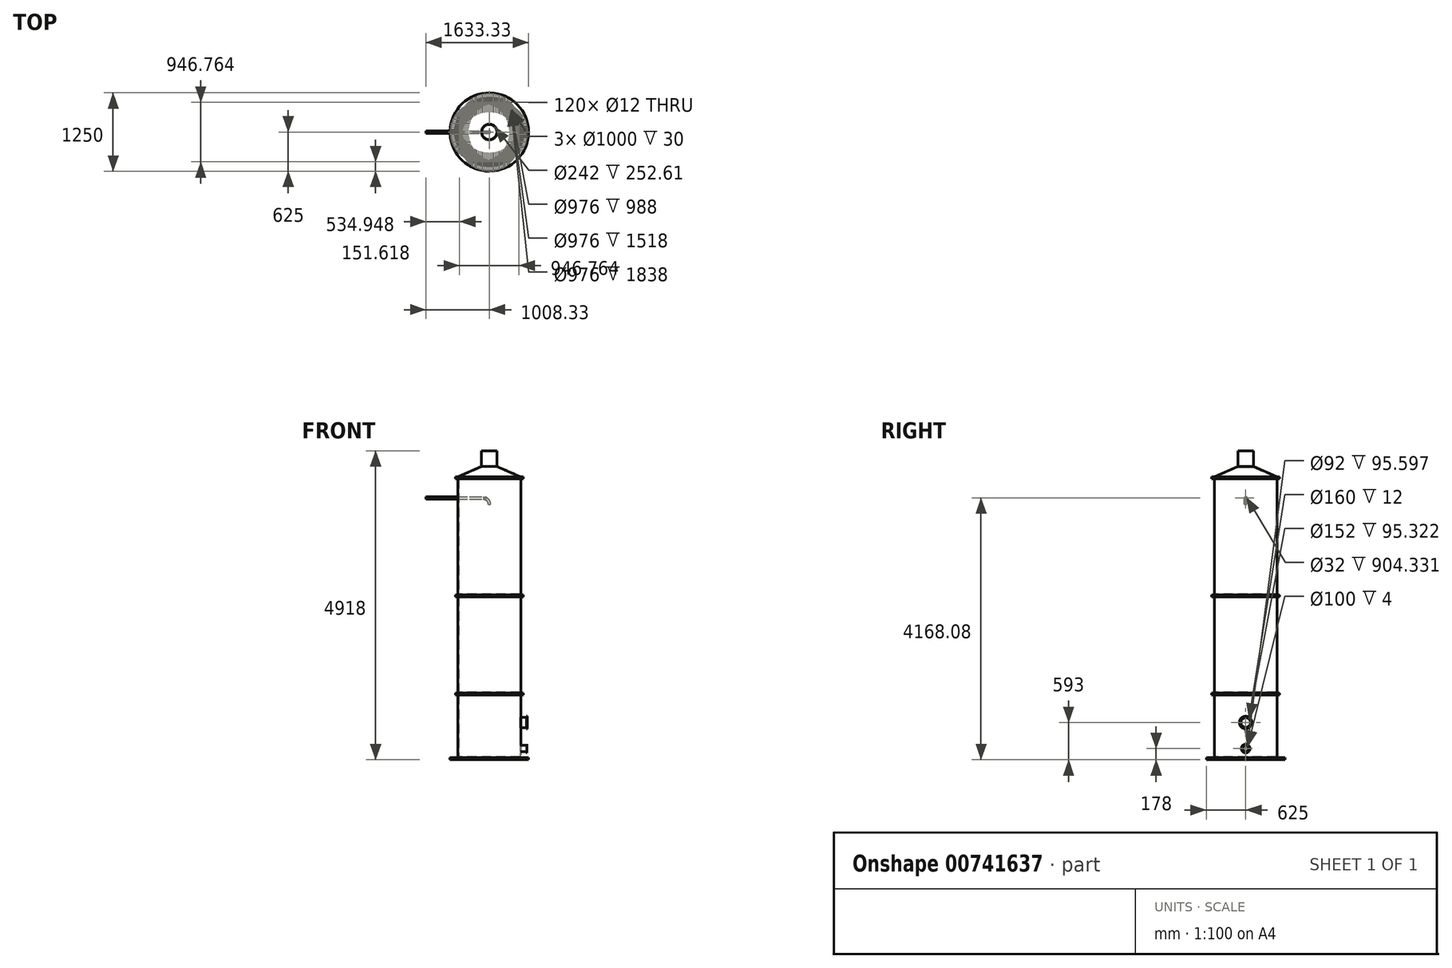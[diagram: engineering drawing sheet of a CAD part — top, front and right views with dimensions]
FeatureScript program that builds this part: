
annotation { "Feature Type Name" : "Feature", "Feature Type Description" : "" }
export const myFeature = defineFeature(function(context is Context, id is Id, definition is map)
    precondition{}
    {
        {
            var Q0;
            Q0=qCreatedBy(makeId("Top.planeOp"),FACE);
            var sketch = newSketch(context, id + "F0", { "sketchPlane" : qUnion([Q0])});
            skCircle(sketch, "E0", {"center": v(0, 0) * mm, "radius": 500 * mm});
            skSolve(sketch);
        }
        {
            var Q0;
            Q0=makeQuery(id+"F0.imprint","IMPRINT",FACE,{"disambiguationData":[TD([[makeQuery(id+"F0.imprint","IMPRINT",EDGE,{"derivedFrom":sQuery(id+"F0.wireOp",EDGE,"E0")}),1.0]])]});
            extrude(context, id + "F1", {"entities" : qUnion([Q0]), "depth" : 1000 * mm, "offsetDistance" : 25 * mm});
        }
        {
            var Q0;
            Q0=makeQuery(id+"F1.opExtrude","CAP_FACE",FACE,{"disambiguationData":[OSD([sQuery(id+"F0.wireOp",EDGE,"E0")])],"isStart":false});
            shell(context, id + "F2", {"entities" : qUnion([Q0]), "thickness" : 12 * mm});
        }
        {
            var Q0;
            {var subQ0=sQuery(id+"F0.wireOp",EDGE,"E0");Q0=makeQuery(id+"F2.opShell","OFFSET_FACE",FACE,{"disambiguationData":[OSD([subQ0]),TDD([makeQuery(id+"F1.opExtrude","CAP_FACE",FACE,{"disambiguationData":[OSD([subQ0])],"isStart":true})])]});}
            cPlane(context, id + "F3", {"entities" : qUnion([Q0]), "cplaneType" : CPlaneType.OFFSET, "offset" : 133 * mm, "width" : 150 * mm, "height" : 150 * mm});
        }
        {
            var Q0;
            Q0=qCreatedBy(id+"F3.planeOp",FACE);
            var sketch = newSketch(context, id + "F4", { "sketchPlane" : qUnion([Q0])});
            skCircle(sketch, "E1", {"center": v(0, 0) * mm, "radius": 500 * mm, "construction": true});
            skLineSegment(sketch, "E2", {"start": v(0, 50) * mm, "end": v(497.5, 50) * mm, "construction": true});
            skLineSegment(sketch, "E3.MirrorCS", {"start": v(0, -50) * mm, "end": v(497.5, -50) * mm, "construction": true});
            skLineSegment(sketch, "E4", {"start": v(497.5, 50) * mm, "end": v(597.5, 50) * mm});
            skLineSegment(sketch, "E5", {"start": v(0, 0) * mm, "end": v(611.46, 0) * mm, "construction": true});
            skArc(sketch, "E6", {"start": v(497.5, 50) * mm, "mid": v(499.37, 25.03) * mm, "end": v(500, 0) * mm});
            skLineSegment(sketch, "E7", {"start": v(500, 0) * mm, "end": v(597.5, 0) * mm});
            skLineSegment(sketch, "E8", {"start": v(597.5, 0) * mm, "end": v(597.5, 50) * mm});
            skSolve(sketch);
        }
        {
            var Q0;
            Q0=makeQuery(id+"F4.imprint","IMPRINT",FACE,{"disambiguationData":[TD([[makeQuery(id+"F4.imprint","IMPRINT",EDGE,{"derivedFrom":sQuery(id+"F4.wireOp",EDGE,"E4")}),-1.0]])]});
            var Q1;
            Q1=sQuery(id+"F4.wireOp",EDGE,"E5");
            revolve(context, id + "F5", {"surfaceOperationType" : NewSurfaceOperationType.NEW, "entities" : qUnion([Q0]), "axis" : qUnion([Q1]), "revolveType" : RevolveType.FULL});
        }
        {
            var Q0;
            Q0=makeQuery(id+"F5.opRevolve","SWEPT_FACE",FACE,{"disambiguationData":[OSD([sQuery(id+"F4.wireOp",EDGE,"E8")])]});
            shell(context, id + "F6", {"entities" : qUnion([Q0]), "thickness" : 4 * mm});
        }
        {
            var Q0;
            Q0=makeQuery(id+"F5.opRevolve","SWEPT_FACE",FACE,{"disambiguationData":[OSD([sQuery(id+"F4.wireOp",EDGE,"E8")])]});
            var sketch = newSketch(context, id + "F7", { "sketchPlane" : qUnion([Q0])});
            skCircle(sketch, "E9.0", {"center": v(0, 145) * mm, "radius": 50 * mm});
            skCircle(sketch, "E10", {"center": v(0, 145) * mm, "radius": 70 * mm});
            skSolve(sketch);
        }
        {
            var Q0;
            Q0=makeQuery(id+"F7.imprint","IMPRINT",FACE,{"disambiguationData":[TD([[makeQuery(id+"F7.imprint","IMPRINT",EDGE,{"derivedFrom":sQuery(id+"F7.wireOp",EDGE,"E9.0")}),1.0]])]});
            var Q1;
            Q1=sQuery(id+"F7.wireOp",EDGE,"E10");
            var Q2;
            Q2=sQuery(id+"F7.wireOp",EDGE,"E9.0");
            extrude(context, id + "F8", {"entities" : qUnion([Q0]), "operationType" : NewBodyOperationType.ADD, "surfaceEntities" : qUnion([Q1, Q2]), "depth" : 4 * mm, "offsetDistance" : 25 * mm});
        }
        {
            var Q0;
            Q0=makeQuery(id+"F1.opExtrude","CAP_FACE",FACE,{"disambiguationData":[OSD([sQuery(id+"F0.wireOp",EDGE,"E0")])],"isStart":true});
            var sketch = newSketch(context, id + "F9", { "sketchPlane" : qUnion([Q0])});
            skCircle(sketch, "E11", {"center": v(0, 0) * mm, "radius": 625 * mm});
            skSolve(sketch);
        }
        {
            var Q0;
            Q0=makeQuery(id+"F9.imprint","IMPRINT",FACE,{"disambiguationData":[TD([[makeQuery(id+"F9.imprint","IMPRINT",EDGE,{"derivedFrom":sQuery(id+"F9.wireOp",EDGE,"E11")}),1.0]])]});
            var Q1;
            Q1=makeQuery(id+"F9.imprint","IMPRINT",FACE,{"disambiguationData":[TD([[makeQuery(id+"F9.imprint","IMPRINT",EDGE,{"derivedFrom":makeQuery(id+"F1.opExtrude","CAP_EDGE",EDGE,{"disambiguationData":[OSD([sQuery(id+"F0.wireOp",EDGE,"E0")])],"isStart":true})}),-1.0]])]});
            var Q2;
            Q2=sQuery(id+"F9.wireOp",EDGE,"E11");
            extrude(context, id + "F10", {"entities" : qUnion([Q0, Q1]), "operationType" : NewBodyOperationType.ADD, "surfaceEntities" : qUnion([Q2]), "depth" : 33 * mm, "offsetDistance" : 25 * mm});
        }
        {
            var Q0;
            Q0=qCreatedBy(id+"F3.planeOp",FACE);
            cPlane(context, id + "F11", {"entities" : qUnion([Q0]), "cplaneType" : CPlaneType.OFFSET, "offset" : 415 * mm, "width" : 150 * mm, "height" : 150 * mm});
        }
        {
            var Q0;
            Q0=qCreatedBy(id+"F11.planeOp",FACE);
            var sketch = newSketch(context, id + "F12", { "sketchPlane" : qUnion([Q0])});
            skCircle(sketch, "E12.0", {"center": v(0, 0) * mm, "radius": 500 * mm});
            skLineSegment(sketch, "E13", {"start": v(0, 0) * mm, "end": v(689.6, 0) * mm, "construction": true});
            skLineSegment(sketch, "E14", {"start": v(0, 80) * mm, "end": v(684.1, 80) * mm, "construction": true});
            skArc(sketch, "E15", {"start": v(493.56, 80) * mm, "mid": v(498.39, 40.13) * mm, "end": v(500, 0) * mm});
            skLineSegment(sketch, "E16", {"start": v(493.56, 80) * mm, "end": v(593.56, 80) * mm});
            skLineSegment(sketch, "E17", {"start": v(593.56, 80) * mm, "end": v(593.56, 0) * mm});
            skLineSegment(sketch, "E18", {"start": v(593.56, 0) * mm, "end": v(500, 0) * mm});
            skSolve(sketch);
        }
        {
            var Q0;
            {var subQ0=sQuery(id+"F12.wireOp",EDGE,"E16");Q0=makeQuery(id+"F12.imprint","IMPRINT",FACE,{"disambiguationData":[TD([[makeQuery(id+"F12.imprint","IMPRINT",EDGE,{"derivedFrom":subQ0}),-1.0]])]});}
            var Q1;
            Q1=sQuery(id+"F12.wireOp",EDGE,"E13");
            revolve(context, id + "F13", {"surfaceOperationType" : NewSurfaceOperationType.NEW, "entities" : qUnion([Q0]), "axis" : qUnion([Q1]), "revolveType" : RevolveType.FULL});
        }
        {
            var Q0;
            Q0=makeQuery(id+"F13.opRevolve","SWEPT_FACE",FACE,{"disambiguationData":[OSD([sQuery(id+"F12.wireOp",EDGE,"E17")])]});
            shell(context, id + "F14", {"entities" : qUnion([Q0]), "thickness" : 4 * mm});
        }
        {
            var Q0;
            Q0=makeQuery(id+"F13.opRevolve","SWEPT_FACE",FACE,{"disambiguationData":[OSD([sQuery(id+"F12.wireOp",EDGE,"E17")])]});
            var sketch = newSketch(context, id + "F15", { "sketchPlane" : qUnion([Q0])});
            skCircle(sketch, "E19", {"center": v(0, 560) * mm, "radius": 100 * mm});
            skSolve(sketch);
        }
        {
            var Q0;
            Q0=makeQuery(id+"F15.imprint","IMPRINT",FACE,{"disambiguationData":[TD([[makeQuery(id+"F15.imprint","IMPRINT",EDGE,{"derivedFrom":sQuery(id+"F15.wireOp",EDGE,"E19")}),1.0]])]});
            extrude(context, id + "F16", {"entities" : qUnion([Q0]), "depth" : 12 * mm, "offsetDistance" : 25 * mm});
        }
        {
            var Q0;
            Q0=makeQuery(id+"F1.opExtrude","CAP_FACE",FACE,{"disambiguationData":[OSD([sQuery(id+"F0.wireOp",EDGE,"E0")])],"isStart":false});
            var sketch = newSketch(context, id + "F17", { "sketchPlane" : qUnion([Q0])});
            skCircle(sketch, "E20", {"center": v(0, 0) * mm, "radius": 540 * mm});
            skCircle(sketch, "E21", {"center": v(0, 0) * mm, "radius": 500 * mm});
            skSolve(sketch);
        }
        {
            var Q0;
            Q0=makeQuery(id+"F17.imprint","IMPRINT",FACE,{"disambiguationData":[TD([[makeQuery(id+"F17.imprint","IMPRINT",EDGE,{"derivedFrom":sQuery(id+"F17.wireOp",EDGE,"E20")}),1.0]])]});
            extrude(context, id + "F18", {"entities" : qUnion([Q0]), "depth" : 30 * mm, "offsetDistance" : 25 * mm});
        }
        {
            var Q0;
            {var subQ0=sQuery(id+"F0.wireOp",EDGE,"E0");Q0=makeQuery(id+"F17.imprint","IMPRINT",FACE,{"disambiguationData":[TD([[makeQuery(id+"F17.imprint","IMPRINT",EDGE,{"derivedFrom":makeQuery(id+"F2.opShell","OFFSET_EDGE",EDGE,{"disambiguationData":[OSD([subQ0]),TDD([makeQuery(id+"F1.opExtrude","CAP_EDGE",EDGE,{"disambiguationData":[OSD([subQ0])],"isStart":false})])]})}),1.0]])]});}
            extrude(context, id + "F19", {"entities" : qUnion([Q0]), "depth" : 12 * mm, "offsetDistance" : 25 * mm});
        }
        {
            var Q0;
            Q0=makeQuery(id+"F19.opExtrude","CAP_FACE",FACE,{"disambiguationData":[OSD([sQuery(id+"F0.wireOp",EDGE,"E0")])],"isStart":false});
            var sketch = newSketch(context, id + "F20", { "sketchPlane" : qUnion([Q0])});
            skLineSegment(sketch, "E22", {"start": v(0, 0) * mm, "end": v(0, 488) * mm, "construction": true});
            skLineSegment(sketch, "E23", {"start": v(0, 0) * mm, "end": v(488, 0) * mm, "construction": true});
            skCircle(sketch, "E24", {"center": v(0, 473.38) * mm, "radius": 6 * mm});
            skCircle(sketch, "E25", {"center": v(0, 0) * mm, "radius": 473.38 * mm, "construction": true});
            skCircle(sketch, "E26.1.0", {"center": v(-24.77, 472.73) * mm, "radius": 6 * mm});
            skCircle(sketch, "E26.2.0", {"center": v(-49.48, 470.79) * mm, "radius": 6 * mm});
            skCircle(sketch, "E26.3.0", {"center": v(-74.05, 467.55) * mm, "radius": 6 * mm});
            skCircle(sketch, "E26.4.0", {"center": v(-98.42, 463.04) * mm, "radius": 6 * mm});
            skCircle(sketch, "E26.5.0", {"center": v(-122.52, 457.25) * mm, "radius": 6 * mm});
            skCircle(sketch, "E26.6.0", {"center": v(-146.28, 450.21) * mm, "radius": 6 * mm});
            skCircle(sketch, "E26.7.0", {"center": v(-169.64, 441.94) * mm, "radius": 6 * mm});
            skCircle(sketch, "E26.8.0", {"center": v(-192.54, 432.46) * mm, "radius": 6 * mm});
            skCircle(sketch, "E26.9.0", {"center": v(-214.91, 421.79) * mm, "radius": 6 * mm});
            skCircle(sketch, "E26.10.0", {"center": v(-236.7, 409.96) * mm, "radius": 6 * mm});
            skCircle(sketch, "E26.11.0", {"center": v(-257.82, 397.01) * mm, "radius": 6 * mm});
            skCircle(sketch, "E26.12.0", {"center": v(-278.25, 382.97) * mm, "radius": 6 * mm});
            skCircle(sketch, "E26.13.0", {"center": v(-297.9, 367.89) * mm, "radius": 6 * mm});
            skCircle(sketch, "E26.14.0", {"center": v(-316.75, 351.8) * mm, "radius": 6 * mm});
            skCircle(sketch, "E26.15.0", {"center": v(-334.73, 334.73) * mm, "radius": 6 * mm});
            skCircle(sketch, "E26.16.0", {"center": v(-351.8, 316.75) * mm, "radius": 6 * mm});
            skCircle(sketch, "E26.17.0", {"center": v(-367.89, 297.9) * mm, "radius": 6 * mm});
            skCircle(sketch, "E26.18.0", {"center": v(-382.97, 278.25) * mm, "radius": 6 * mm});
            skCircle(sketch, "E26.19.0", {"center": v(-397.01, 257.82) * mm, "radius": 6 * mm});
            skCircle(sketch, "E26.20.0", {"center": v(-409.96, 236.7) * mm, "radius": 6 * mm});
            skCircle(sketch, "E26.21.0", {"center": v(-421.79, 214.91) * mm, "radius": 6 * mm});
            skCircle(sketch, "E26.22.0", {"center": v(-432.46, 192.54) * mm, "radius": 6 * mm});
            skCircle(sketch, "E26.23.0", {"center": v(-441.94, 169.64) * mm, "radius": 6 * mm});
            skCircle(sketch, "E26.24.0", {"center": v(-450.21, 146.28) * mm, "radius": 6 * mm});
            skCircle(sketch, "E26.25.0", {"center": v(-457.25, 122.52) * mm, "radius": 6 * mm});
            skCircle(sketch, "E26.26.0", {"center": v(-463.04, 98.42) * mm, "radius": 6 * mm});
            skCircle(sketch, "E26.27.0", {"center": v(-467.55, 74.05) * mm, "radius": 6 * mm});
            skCircle(sketch, "E26.28.0", {"center": v(-470.79, 49.48) * mm, "radius": 6 * mm});
            skCircle(sketch, "E26.29.0", {"center": v(-472.73, 24.77) * mm, "radius": 6 * mm});
            skCircle(sketch, "E26.30.0", {"center": v(-473.38, 0) * mm, "radius": 6 * mm});
            skCircle(sketch, "E26.31.0", {"center": v(-472.73, -24.77) * mm, "radius": 6 * mm});
            skCircle(sketch, "E26.32.0", {"center": v(-470.79, -49.48) * mm, "radius": 6 * mm});
            skCircle(sketch, "E26.33.0", {"center": v(-467.55, -74.05) * mm, "radius": 6 * mm});
            skCircle(sketch, "E26.34.0", {"center": v(-463.04, -98.42) * mm, "radius": 6 * mm});
            skCircle(sketch, "E26.35.0", {"center": v(-457.25, -122.52) * mm, "radius": 6 * mm});
            skCircle(sketch, "E26.36.0", {"center": v(-450.21, -146.28) * mm, "radius": 6 * mm});
            skCircle(sketch, "E26.37.0", {"center": v(-441.94, -169.64) * mm, "radius": 6 * mm});
            skCircle(sketch, "E26.38.0", {"center": v(-432.46, -192.54) * mm, "radius": 6 * mm});
            skCircle(sketch, "E26.39.0", {"center": v(-421.79, -214.91) * mm, "radius": 6 * mm});
            skCircle(sketch, "E26.40.0", {"center": v(-409.96, -236.7) * mm, "radius": 6 * mm});
            skCircle(sketch, "E26.41.0", {"center": v(-397.01, -257.82) * mm, "radius": 6 * mm});
            skCircle(sketch, "E26.42.0", {"center": v(-382.97, -278.25) * mm, "radius": 6 * mm});
            skCircle(sketch, "E26.43.0", {"center": v(-367.89, -297.9) * mm, "radius": 6 * mm});
            skCircle(sketch, "E26.44.0", {"center": v(-351.8, -316.75) * mm, "radius": 6 * mm});
            skCircle(sketch, "E26.45.0", {"center": v(-334.73, -334.73) * mm, "radius": 6 * mm});
            skCircle(sketch, "E26.46.0", {"center": v(-316.75, -351.8) * mm, "radius": 6 * mm});
            skCircle(sketch, "E26.47.0", {"center": v(-297.9, -367.89) * mm, "radius": 6 * mm});
            skCircle(sketch, "E26.48.0", {"center": v(-278.25, -382.97) * mm, "radius": 6 * mm});
            skCircle(sketch, "E26.49.0", {"center": v(-257.82, -397.01) * mm, "radius": 6 * mm});
            skCircle(sketch, "E26.50.0", {"center": v(-236.7, -409.96) * mm, "radius": 6 * mm});
            skCircle(sketch, "E26.51.0", {"center": v(-214.91, -421.79) * mm, "radius": 6 * mm});
            skCircle(sketch, "E26.52.0", {"center": v(-192.54, -432.46) * mm, "radius": 6 * mm});
            skCircle(sketch, "E26.53.0", {"center": v(-169.64, -441.94) * mm, "radius": 6 * mm});
            skCircle(sketch, "E26.54.0", {"center": v(-146.28, -450.21) * mm, "radius": 6 * mm});
            skCircle(sketch, "E26.55.0", {"center": v(-122.52, -457.25) * mm, "radius": 6 * mm});
            skCircle(sketch, "E26.56.0", {"center": v(-98.42, -463.04) * mm, "radius": 6 * mm});
            skCircle(sketch, "E26.57.0", {"center": v(-74.05, -467.55) * mm, "radius": 6 * mm});
            skCircle(sketch, "E26.58.0", {"center": v(-49.48, -470.79) * mm, "radius": 6 * mm});
            skCircle(sketch, "E26.59.0", {"center": v(-24.77, -472.73) * mm, "radius": 6 * mm});
            skCircle(sketch, "E26.60.0", {"center": v(0, -473.38) * mm, "radius": 6 * mm});
            skCircle(sketch, "E26.61.0", {"center": v(24.77, -472.73) * mm, "radius": 6 * mm});
            skCircle(sketch, "E26.62.0", {"center": v(49.48, -470.79) * mm, "radius": 6 * mm});
            skCircle(sketch, "E26.63.0", {"center": v(74.05, -467.55) * mm, "radius": 6 * mm});
            skCircle(sketch, "E26.64.0", {"center": v(98.42, -463.04) * mm, "radius": 6 * mm});
            skCircle(sketch, "E26.65.0", {"center": v(122.52, -457.25) * mm, "radius": 6 * mm});
            skCircle(sketch, "E26.66.0", {"center": v(146.28, -450.21) * mm, "radius": 6 * mm});
            skCircle(sketch, "E26.67.0", {"center": v(169.64, -441.94) * mm, "radius": 6 * mm});
            skCircle(sketch, "E26.68.0", {"center": v(192.54, -432.46) * mm, "radius": 6 * mm});
            skCircle(sketch, "E26.69.0", {"center": v(214.91, -421.79) * mm, "radius": 6 * mm});
            skCircle(sketch, "E26.70.0", {"center": v(236.7, -409.96) * mm, "radius": 6 * mm});
            skCircle(sketch, "E26.71.0", {"center": v(257.82, -397.01) * mm, "radius": 6 * mm});
            skCircle(sketch, "E26.72.0", {"center": v(278.25, -382.97) * mm, "radius": 6 * mm});
            skCircle(sketch, "E26.73.0", {"center": v(297.9, -367.89) * mm, "radius": 6 * mm});
            skCircle(sketch, "E26.74.0", {"center": v(316.75, -351.8) * mm, "radius": 6 * mm});
            skCircle(sketch, "E26.75.0", {"center": v(334.73, -334.73) * mm, "radius": 6 * mm});
            skCircle(sketch, "E26.76.0", {"center": v(351.8, -316.75) * mm, "radius": 6 * mm});
            skCircle(sketch, "E26.77.0", {"center": v(367.89, -297.9) * mm, "radius": 6 * mm});
            skCircle(sketch, "E26.78.0", {"center": v(382.97, -278.25) * mm, "radius": 6 * mm});
            skCircle(sketch, "E26.79.0", {"center": v(397.01, -257.82) * mm, "radius": 6 * mm});
            skCircle(sketch, "E26.80.0", {"center": v(409.96, -236.7) * mm, "radius": 6 * mm});
            skCircle(sketch, "E26.81.0", {"center": v(421.79, -214.91) * mm, "radius": 6 * mm});
            skCircle(sketch, "E26.82.0", {"center": v(432.46, -192.54) * mm, "radius": 6 * mm});
            skCircle(sketch, "E26.83.0", {"center": v(441.94, -169.64) * mm, "radius": 6 * mm});
            skCircle(sketch, "E26.84.0", {"center": v(450.21, -146.28) * mm, "radius": 6 * mm});
            skCircle(sketch, "E26.85.0", {"center": v(457.25, -122.52) * mm, "radius": 6 * mm});
            skCircle(sketch, "E26.86.0", {"center": v(463.04, -98.42) * mm, "radius": 6 * mm});
            skCircle(sketch, "E26.87.0", {"center": v(467.55, -74.05) * mm, "radius": 6 * mm});
            skCircle(sketch, "E26.88.0", {"center": v(470.79, -49.48) * mm, "radius": 6 * mm});
            skCircle(sketch, "E26.89.0", {"center": v(472.73, -24.77) * mm, "radius": 6 * mm});
            skCircle(sketch, "E26.90.0", {"center": v(473.38, 0) * mm, "radius": 6 * mm});
            skCircle(sketch, "E26.91.0", {"center": v(472.73, 24.77) * mm, "radius": 6 * mm});
            skCircle(sketch, "E26.92.0", {"center": v(470.79, 49.48) * mm, "radius": 6 * mm});
            skCircle(sketch, "E26.93.0", {"center": v(467.55, 74.05) * mm, "radius": 6 * mm});
            skCircle(sketch, "E26.94.0", {"center": v(463.04, 98.42) * mm, "radius": 6 * mm});
            skCircle(sketch, "E26.95.0", {"center": v(457.25, 122.52) * mm, "radius": 6 * mm});
            skCircle(sketch, "E26.96.0", {"center": v(450.21, 146.28) * mm, "radius": 6 * mm});
            skCircle(sketch, "E26.97.0", {"center": v(441.94, 169.64) * mm, "radius": 6 * mm});
            skCircle(sketch, "E26.98.0", {"center": v(432.46, 192.54) * mm, "radius": 6 * mm});
            skCircle(sketch, "E26.99.0", {"center": v(421.79, 214.91) * mm, "radius": 6 * mm});
            skCircle(sketch, "E26.100.0", {"center": v(409.96, 236.7) * mm, "radius": 6 * mm});
            skCircle(sketch, "E26.101.0", {"center": v(397.01, 257.82) * mm, "radius": 6 * mm});
            skCircle(sketch, "E26.102.0", {"center": v(382.97, 278.25) * mm, "radius": 6 * mm});
            skCircle(sketch, "E26.103.0", {"center": v(367.89, 297.9) * mm, "radius": 6 * mm});
            skCircle(sketch, "E26.104.0", {"center": v(351.8, 316.75) * mm, "radius": 6 * mm});
            skCircle(sketch, "E26.105.0", {"center": v(334.73, 334.73) * mm, "radius": 6 * mm});
            skCircle(sketch, "E26.106.0", {"center": v(316.75, 351.8) * mm, "radius": 6 * mm});
            skCircle(sketch, "E26.107.0", {"center": v(297.9, 367.89) * mm, "radius": 6 * mm});
            skCircle(sketch, "E26.108.0", {"center": v(278.25, 382.97) * mm, "radius": 6 * mm});
            skCircle(sketch, "E26.109.0", {"center": v(257.82, 397.01) * mm, "radius": 6 * mm});
            skCircle(sketch, "E26.110.0", {"center": v(236.7, 409.96) * mm, "radius": 6 * mm});
            skCircle(sketch, "E26.111.0", {"center": v(214.91, 421.79) * mm, "radius": 6 * mm});
            skCircle(sketch, "E26.112.0", {"center": v(192.54, 432.46) * mm, "radius": 6 * mm});
            skCircle(sketch, "E26.113.0", {"center": v(169.64, 441.94) * mm, "radius": 6 * mm});
            skCircle(sketch, "E26.114.0", {"center": v(146.28, 450.21) * mm, "radius": 6 * mm});
            skCircle(sketch, "E26.115.0", {"center": v(122.52, 457.25) * mm, "radius": 6 * mm});
            skCircle(sketch, "E26.116.0", {"center": v(98.42, 463.04) * mm, "radius": 6 * mm});
            skCircle(sketch, "E26.117.0", {"center": v(74.05, 467.55) * mm, "radius": 6 * mm});
            skCircle(sketch, "E26.118.0", {"center": v(49.48, 470.79) * mm, "radius": 6 * mm});
            skCircle(sketch, "E26.119.0", {"center": v(24.77, 472.73) * mm, "radius": 6 * mm});
            skSolve(sketch);
        }
        {
            var Q0;
            Q0 = qSketchRegion(id + "F20", true);
            extrude(context, id + "F21", {"entities" : qUnion([Q0]), "operationType" : NewBodyOperationType.REMOVE, "oppositeDirection" : true, "depth" : 40 * mm, "offsetDistance" : 25 * mm});
        }
        {
            var Q0;
            Q0=makeQuery(id+"F18.opExtrude","CAP_FACE",FACE,{"disambiguationData":[OSD([sQuery(id+"F17.wireOp",EDGE,"E20"),sQuery(id+"F17.wireOp",EDGE,"E21")])],"isStart":false});
            var sketch = newSketch(context, id + "F22", { "sketchPlane" : qUnion([Q0])});
            skCircle(sketch, "E27", {"center": v(0, 0) * mm, "radius": 500 * mm});
            skSolve(sketch);
        }
        {
            var Q0;
            Q0=makeQuery(id+"F22.imprint","IMPRINT",FACE,{"disambiguationData":[TD([[makeQuery(id+"F22.imprint","IMPRINT",EDGE,{"derivedFrom":sQuery(id+"F22.wireOp",EDGE,"E27")}),1.0]])]});
            extrude(context, id + "F23", {"entities" : qUnion([Q0]), "depth" : 1500 * mm, "offsetDistance" : 25 * mm});
        }
        {
            var Q0;
            Q0=makeQuery(id+"F23.opExtrude","CAP_FACE",FACE,{"disambiguationData":[OSD([sQuery(id+"F22.wireOp",EDGE,"E27")])],"isStart":false});
            shell(context, id + "F24", {"entities" : qUnion([Q0]), "thickness" : 12 * mm});
        }
        {
            var Q0;
            Q0=makeQuery(id+"F23.opExtrude","CAP_FACE",FACE,{"disambiguationData":[OSD([sQuery(id+"F22.wireOp",EDGE,"E27")])],"isStart":false});
            var sketch = newSketch(context, id + "F25", { "sketchPlane" : qUnion([Q0])});
            skCircle(sketch, "E28", {"center": v(0, 0) * mm, "radius": 540 * mm});
            skCircle(sketch, "E29", {"center": v(0, 0) * mm, "radius": 500 * mm});
            skSolve(sketch);
        }
        {
            var Q0;
            Q0=makeQuery(id+"F25.imprint","IMPRINT",FACE,{"disambiguationData":[TD([[makeQuery(id+"F25.imprint","IMPRINT",EDGE,{"derivedFrom":sQuery(id+"F25.wireOp",EDGE,"E29")}),1.0]])]});
            extrude(context, id + "F26", {"entities" : qUnion([Q0]), "operationType" : NewBodyOperationType.ADD, "depth" : 30 * mm, "offsetDistance" : 25 * mm});
        }
        {
            var Q0;
            Q0=makeQuery(id+"F26.opExtrude","CAP_FACE",FACE,{"disambiguationData":[OSD([sQuery(id+"F22.wireOp",EDGE,"E27"),sQuery(id+"F25.wireOp",EDGE,"E29")])],"isStart":false});
            var sketch = newSketch(context, id + "F27", { "sketchPlane" : qUnion([Q0])});
            skCircle(sketch, "E30", {"center": v(0, 0) * mm, "radius": 540 * mm});
            skCircle(sketch, "E31", {"center": v(0, 0) * mm, "radius": 494 * mm});
            skSolve(sketch);
        }
        {
            var Q0;
            Q0=makeQuery(id+"F27.imprint","IMPRINT",FACE,{"disambiguationData":[TD([[makeQuery(id+"F27.imprint","IMPRINT",EDGE,{"derivedFrom":sQuery(id+"F27.wireOp",EDGE,"E30")}),1.0]])]});
            extrude(context, id + "F28", {"entities" : qUnion([Q0]), "depth" : 30 * mm, "offsetDistance" : 25 * mm});
        }
        {
            var Q0;
            Q0=makeQuery(id+"F28.opExtrude","CAP_FACE",FACE,{"disambiguationData":[OSD([sQuery(id+"F25.wireOp",EDGE,"E29"),sQuery(id+"F27.wireOp",EDGE,"E30")])],"isStart":false});
            var sketch = newSketch(context, id + "F29", { "sketchPlane" : qUnion([Q0])});
            skCircle(sketch, "E32", {"center": v(0, 0) * mm, "radius": 500 * mm});
            skSolve(sketch);
        }
        {
            var Q0;
            Q0=makeQuery(id+"F29.imprint","IMPRINT",FACE,{"disambiguationData":[TD([[makeQuery(id+"F29.imprint","IMPRINT",EDGE,{"derivedFrom":sQuery(id+"F29.wireOp",EDGE,"E32")}),1.0]])]});
            extrude(context, id + "F30", {"entities" : qUnion([Q0]), "depth" : 1850 * mm, "offsetDistance" : 25 * mm});
        }
        {
            var Q0;
            Q0=makeQuery(id+"F30.opExtrude","CAP_FACE",FACE,{"disambiguationData":[OSD([sQuery(id+"F29.wireOp",EDGE,"E32")])],"isStart":false});
            shell(context, id + "F31", {"entities" : qUnion([Q0]), "thickness" : 12 * mm});
        }
        {
            var Q0;
            Q0=makeQuery(id+"F30.opExtrude","CAP_FACE",FACE,{"disambiguationData":[OSD([sQuery(id+"F29.wireOp",EDGE,"E32")])],"isStart":false});
            var sketch = newSketch(context, id + "F32", { "sketchPlane" : qUnion([Q0])});
            skCircle(sketch, "E33", {"center": v(0, 0) * mm, "radius": 540 * mm});
            skCircle(sketch, "E34", {"center": v(0, 0) * mm, "radius": 494 * mm});
            skSolve(sketch);
        }
        {
            var Q0;
            Q0=makeQuery(id+"F32.imprint","IMPRINT",FACE,{"disambiguationData":[TD([[makeQuery(id+"F32.imprint","IMPRINT",EDGE,{"derivedFrom":sQuery(id+"F32.wireOp",EDGE,"E33")}),1.0]])]});
            var Q1;
            Q1=sQuery(id+"F32.wireOp",EDGE,"E33");
            var Q2;
            Q2=sQuery(id+"F32.wireOp",EDGE,"E34");
            extrude(context, id + "F33", {"entities" : qUnion([Q0]), "surfaceEntities" : qUnion([Q1, Q2]), "depth" : 30 * mm, "offsetDistance" : 25 * mm});
        }
        {
            var Q0;
            Q0=makeQuery(id+"F33.opExtrude","CAP_FACE",FACE,{"disambiguationData":[OSD([sQuery(id+"F29.wireOp",EDGE,"E32"),sQuery(id+"F32.wireOp",EDGE,"E33")])],"isStart":false});
            var sketch = newSketch(context, id + "F34", { "sketchPlane" : qUnion([Q0])});
            skCircle(sketch, "E35", {"center": v(0, 0) * mm, "radius": 500 * mm});
            skSolve(sketch);
        }
        {
            var Q0;
            Q0=makeQuery(id+"F34.imprint","IMPRINT",FACE,{"disambiguationData":[TD([[makeQuery(id+"F34.imprint","IMPRINT",EDGE,{"derivedFrom":sQuery(id+"F34.wireOp",EDGE,"E35")}),-1.0]])]});
            cPlane(context, id + "F35", {"entities" : qUnion([Q0]), "cplaneType" : CPlaneType.OFFSET, "offset" : 165 * mm, "width" : 150 * mm, "height" : 150 * mm});
        }
        {
            var Q0;
            Q0=qCreatedBy(id+"F35.planeOp",FACE);
            var sketch = newSketch(context, id + "F36", { "sketchPlane" : qUnion([Q0])});
            skCircle(sketch, "E36", {"center": v(0, 0) * mm, "radius": 125 * mm});
            skSolve(sketch);
        }
        {
            var Q0;
            Q0=makeQuery(id+"F34.imprint","IMPRINT",FACE,{"disambiguationData":[TD([[makeQuery(id+"F34.imprint","IMPRINT",EDGE,{"derivedFrom":sQuery(id+"F34.wireOp",EDGE,"E35")}),1.0]])]});
            var Q1;
            Q1=makeQuery(id+"F36.imprint","IMPRINT",FACE,{"disambiguationData":[TD([[makeQuery(id+"F36.imprint","IMPRINT",EDGE,{"derivedFrom":sQuery(id+"F36.wireOp",EDGE,"E36")}),1.0]])]});
            loft(context, id + "F37", {"sheetProfilesArray" : [{ "sheetProfileEntities" : qUnion([Q0]) }, { "sheetProfileEntities" : qUnion([Q1]) }]});
        }
        {
            var Q0;
            Q0=makeQuery(id+"F37.opLoft","CAP_FACE",FACE,{"disambiguationData":[OSD([makeQuery(id+"F34.imprint","IMPRINT",FACE,{"disambiguationData":[TD([[makeQuery(id+"F34.imprint","IMPRINT",EDGE,{"derivedFrom":sQuery(id+"F34.wireOp",EDGE,"E35")}),1.0]])]})])],"isStart":true});
            shell(context, id + "F38", {"entities" : qUnion([Q0]), "thickness" : 12 * mm});
        }
        {
            var Q0;
            Q0=makeQuery(id+"F37.opLoft","CAP_FACE",FACE,{"disambiguationData":[OSD([makeQuery(id+"F36.imprint","IMPRINT",FACE,{"disambiguationData":[TD([[makeQuery(id+"F36.imprint","IMPRINT",EDGE,{"derivedFrom":sQuery(id+"F36.wireOp",EDGE,"E36")}),1.0]])]})])],"isStart":true});
            var sketch = newSketch(context, id + "F39", { "sketchPlane" : qUnion([Q0])});
            skCircle(sketch, "E37.0", {"center": v(0, 0) * mm, "radius": 125 * mm});
            skSolve(sketch);
        }
        {
            var Q0;
            Q0=makeQuery(id+"F39.imprint","IMPRINT",FACE,{"disambiguationData":[TD([[makeQuery(id+"F39.imprint","IMPRINT",EDGE,{"derivedFrom":sQuery(id+"F39.wireOp",EDGE,"E37.0")}),1.0]])]});
            extrude(context, id + "F40", {"entities" : qUnion([Q0]), "operationType" : NewBodyOperationType.ADD, "depth" : 250 * mm, "offsetDistance" : 25 * mm});
        }
        {
            var Q0;
            Q0=makeQuery(id+"F40.opExtrude","CAP_FACE",FACE,{"disambiguationData":[OSD([sQuery(id+"F39.wireOp",EDGE,"E37.0")])],"isStart":false});
            shell(context, id + "F41", {"entities" : qUnion([Q0]), "thickness" : 4 * mm});
        }
        {
            var Q0;
            Q0=qCreatedBy(id+"F35.planeOp",FACE);
            cPlane(context, id + "F42", {"entities" : qUnion([Q0]), "cplaneType" : CPlaneType.OFFSET, "offset" : 500 * mm, "oppositeDirection" : true, "width" : 150 * mm, "height" : 150 * mm});
        }
        {
            var Q0;
            Q0=qCreatedBy(id+"F42.planeOp",FACE);
            var sketch = newSketch(context, id + "F43", { "sketchPlane" : qUnion([Q0])});
            skLineSegment(sketch, "E38", {"start": v(-747.05, 0) * mm, "end": v(862.3, 0) * mm, "construction": true});
            skSolve(sketch);
        }
        {
            var Q0;
            Q0=qCreatedBy(makeId("Front.planeOp"),FACE);
            var sketch = newSketch(context, id + "F44", { "sketchPlane" : qUnion([Q0])});
            skLineSegment(sketch, "E39", {"start": v(0, 3117.65) * mm, "end": v(0, 4419.03) * mm, "construction": true});
            skLineSegment(sketch, "E40.0", {"start": v(-747.05, 4135) * mm, "end": v(862.3, 4135) * mm, "construction": true});
            skLineSegment(sketch, "E41", {"start": v(-100, 4135) * mm, "end": v(-1008.33, 4135) * mm});
            skLineSegment(sketch, "E42", {"start": v(0, 4035) * mm, "end": v(0, 3775) * mm});
            skArc(sketch, "E43", {"start": v(0, 4035) * mm, "mid": v(-29.29, 4105.71) * mm, "end": v(-100, 4135) * mm});
            skSolve(sketch);
        }
        {
            var Q0;
            Q0=sQuery(id+"F44.wireOp",VERTEX,"E41.end");
            var Q1;
            Q1=qCreatedBy(makeId("Right.planeOp"),FACE);
            cPlane(context, id + "F45", {"entities" : qUnion([Q0, Q1]), "cplaneType" : CPlaneType.PLANE_POINT, "offset" : 25 * mm, "width" : 150 * mm, "height" : 150 * mm});
        }
        {
            var Q0;
            Q0=qCreatedBy(id+"F45.planeOp",FACE);
            var sketch = newSketch(context, id + "F46", { "sketchPlane" : qUnion([Q0])});
            skCircle(sketch, "E44", {"center": v(0, 4135.08) * mm, "radius": 20 * mm});
            skSolve(sketch);
        }
        {
            var Q0;
            Q0=makeQuery(id+"F46.imprint","IMPRINT",FACE,{"disambiguationData":[TD([[makeQuery(id+"F46.imprint","IMPRINT",EDGE,{"derivedFrom":sQuery(id+"F46.wireOp",EDGE,"E44")}),1.0]])]});
            var Q1;
            Q1=sQuery(id+"F44.wireOp",EDGE,"E41");
            var Q2;
            Q2=sQuery(id+"F44.wireOp",EDGE,"E43");
            sweep(context, id + "F47", {"profiles" : qUnion([Q0]), "path" : qUnion([Q1, Q2])});
        }
        {
            var Q0;
            Q0=makeQuery(id+"F47.opSweep","CAP_FACE",FACE,{"disambiguationData":[OSD([sQuery(id+"F44.wireOp",VERTEX,"E43.start"),sQuery(id+"F46.wireOp",EDGE,"E44")])],"isStart":false});
            shell(context, id + "F48", {"entities" : qUnion([Q0]), "thickness" : 4 * mm});
        }
    });
